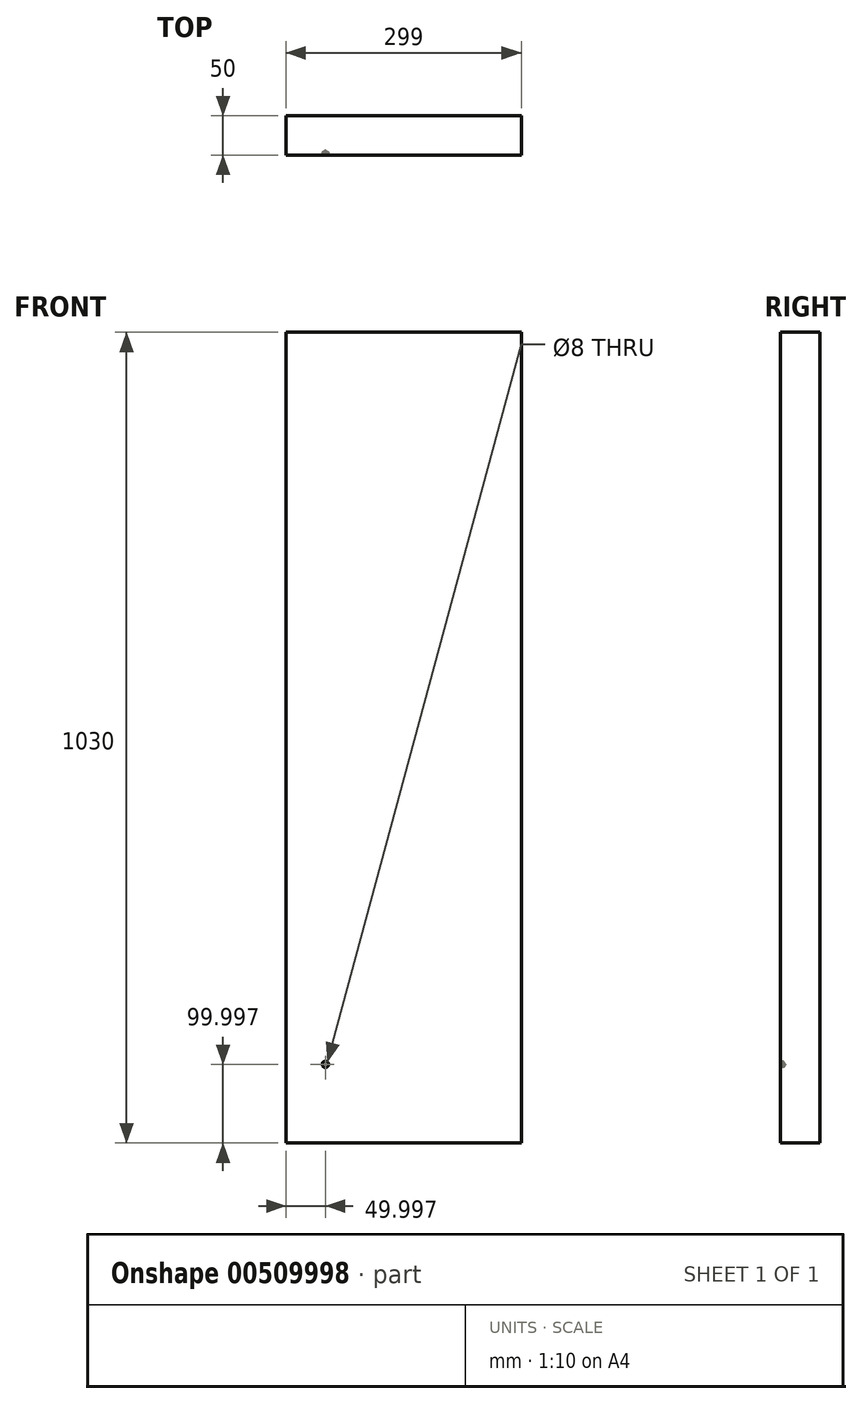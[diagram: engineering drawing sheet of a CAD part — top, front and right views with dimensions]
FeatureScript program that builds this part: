
annotation { "Feature Type Name" : "Feature", "Feature Type Description" : "" }
export const myFeature = defineFeature(function(context is Context, id is Id, definition is map)
    precondition{}
    {
        {
            var Q0;
            Q0=qCreatedBy(makeId("Front.planeOp"),FACE);
            var sketch = newSketch(context, id + "F0", { "sketchPlane" : qUnion([Q0])});
            skLineSegment(sketch, "E0.bottom", {"start": v(-265.45, 963.84) * mm, "end": v(33.55, 963.84) * mm});
            skLineSegment(sketch, "E0.top", {"start": v(-265.45, -66.16) * mm, "end": v(33.55, -66.16) * mm});
            skLineSegment(sketch, "E0.left", {"start": v(-265.45, 963.84) * mm, "end": v(-265.45, -66.16) * mm});
            skLineSegment(sketch, "E0.right", {"start": v(33.55, 963.84) * mm, "end": v(33.55, -66.16) * mm});
            skSolve(sketch);
        }
        {
            var Q0;
            Q0=makeQuery(id+"F0.imprint","IMPRINT",FACE,{"disambiguationData":[TD([[makeQuery(id+"F0.imprint","IMPRINT",EDGE,{"derivedFrom":sQuery(id+"F0.wireOp",EDGE,"E0.bottom")}),-1.0]])]});
            extrude(context, id + "F1", {"entities" : qUnion([Q0]), "depth" : 50 * mm});
        }
        {
            var Q0;
            Q0=makeQuery(id+"F1.opExtrude","CAP_FACE",FACE,{"disambiguationData":[OSD([sQuery(id+"F0.wireOp",EDGE,"E0.bottom"),sQuery(id+"F0.wireOp",EDGE,"E0.top"),sQuery(id+"F0.wireOp",EDGE,"E0.left"),sQuery(id+"F0.wireOp",EDGE,"E0.right")])],"isStart":false});
            var sketch = newSketch(context, id + "F2", { "sketchPlane" : qUnion([Q0])});
            skCircle(sketch, "E1", {"center": v(-215.45, 33.84) * mm, "radius": 4 * mm});
            skSolve(sketch);
        }
        {
            var Q0;
            Q0=sQuery(id+"F2.wireOp",VERTEX,"E1.center");
            var Q1;
            Q1=makeQuery(id+"F1.opExtrude","SWEPT_BODY",BODY,{"disambiguationData":[OSD([sQuery(id+"F0.wireOp",EDGE,"E0.bottom"),sQuery(id+"F0.wireOp",EDGE,"E0.top"),sQuery(id+"F0.wireOp",EDGE,"E0.left"),sQuery(id+"F0.wireOp",EDGE,"E0.right")])]});
            hole(context, id + "F3", {"style" : HoleStyle.SIMPLE, "endStyle" : HoleEndStyle.BLIND, "holeDiameter" : 8 * mm, "holeDepth" : 4 * mm, "isTappedThrough" : true, "tappedDepth" : 12 * mm, "tapClearance" : 3, "locations" : qUnion([Q0]), "scope" : qUnion([Q1])});
        }
    });
